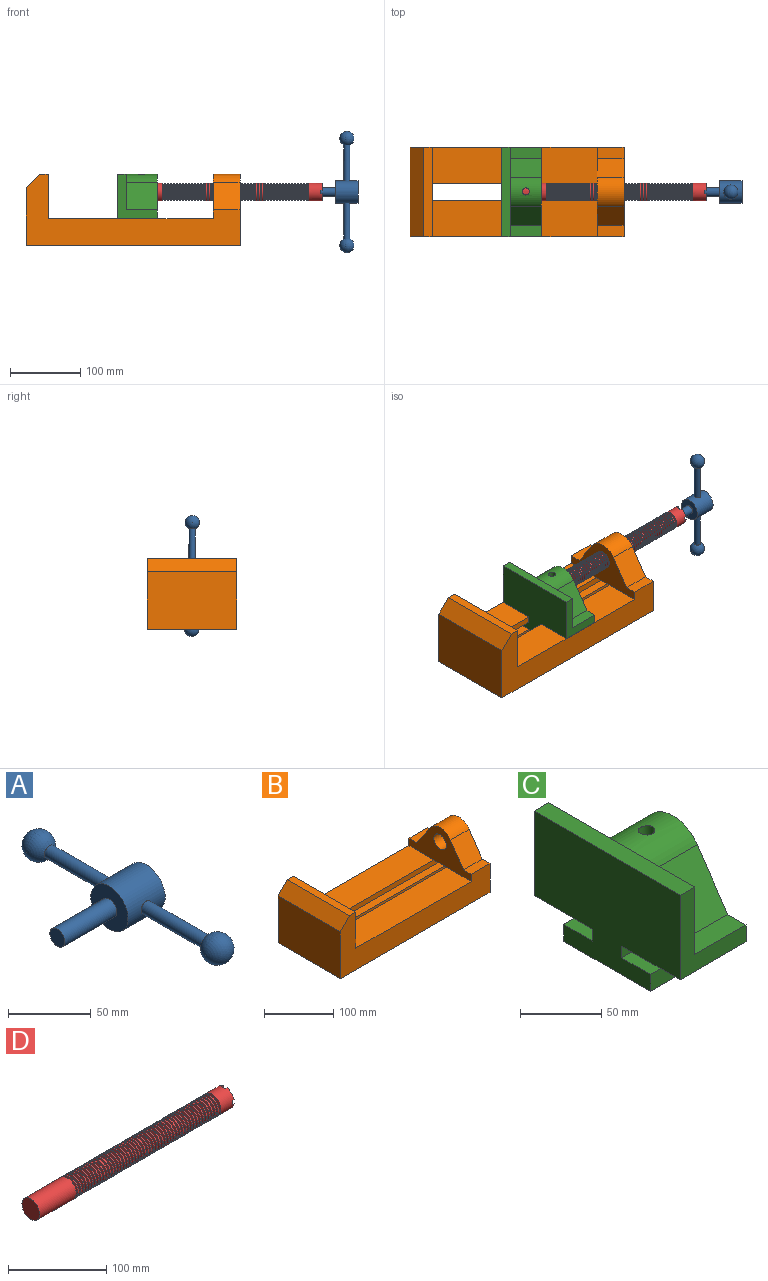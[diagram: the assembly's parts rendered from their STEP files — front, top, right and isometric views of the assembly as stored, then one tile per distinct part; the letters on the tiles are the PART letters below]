
ASSEMBLY  parts=4 mates=3
PART A: 13 faces, bbox 76.2x172.7x31.8 mm
  f0: cylinder r=4.45mm len=51.82mm, axis (0,1,0), area 1438.5mm2, adj f1,f8
  f1: cylinder r=15.88mm len=31.75mm, axis (-1,0,0), area 3041.6mm2, adj f0,f4,f5,f6
  f2: cylinder r=6.35mm len=44.45mm, axis (-1,0,0), area 1773.5mm2, adj f3,f5
  f3: plane 12.7x12.7mm, normal (-1,0,0), area 126.7mm2, adj f2
  f4: plane 31.75x31.75mm, normal (1,0,0), area 791.7mm2, adj f1
  f5: plane 31.75x31.75mm, normal (-1,0,0), area 665.1mm2, adj f1,f2
  f6: cylinder r=4.45mm len=51.82mm, axis (0,1,0), area 1438.5mm2, adj f1,f7
  f7: sphere r=10.16mm, area 1231.8mm2, adj f6
  f8: sphere r=10.16mm, area 1231.8mm2, adj f0
  f9: sphere r=4.45mm, area 124.1mm2, adj f10
  f10: plane 8.89x8.89mm, normal (0,-1,0), area 62.1mm2, adj f9
  f11: sphere r=4.45mm, area 124.1mm2, adj f12
  f12: plane 8.89x8.89mm, normal (0,1,0), area 62.1mm2, adj f11
PART B: 28 faces, bbox 304.8x127x101.6 mm
  f0: plane 234.95x50.8mm, normal (0,0,1), area 11935.5mm2, adj f5,f9,f16,f22
  f1: plane 234.95x50.8mm, normal (0,0,1), area 11935.5mm2, adj f5,f8,f16,f23
  f2: plane 127x82.55mm, normal (-1,0,0), area 10483.8mm2, adj f3,f7,f8,f9
  f3: plane 304.8x127mm, normal (0,0,-1), area 31774.1mm2, adj f2,f4,f5,f8,f9,f18,f27
  f4: plane 127x101.27mm, normal (1,0,0), area 7370.6mm2, adj f3,f8,f9,f10,f11,f12,f13,f14
  f5: plane 127x101.6mm, normal (1,0,0), area 9667.6mm2, adj f0,f1,f3,f6,f8,f9,f18,f19
  f6: plane 127x12.7mm, normal (0,0,1), area 1612.9mm2, adj f5,f7,f8,f9
  f7: plane 127x19.05mm, normal (-0.71,0,0.71), area 3421.5mm2, adj f2,f6,f8,f9
  f8: plane 304.8x101.6mm, normal (0,-1,0), area 13931.4mm2, adj f1,f2,f3,f4,f5,f6,f7,f14
  f9: plane 304.8x101.6mm, normal (0,1,0), area 13931.4mm2, adj f0,f2,f3,f4,f5,f6,f7,f10
  f10: plane 38.1x15.91mm, normal (0,0,1), area 606.2mm2, adj f4,f9,f11,f16
  f11: plane 39.29x38.1mm, normal (0,0.83,0.56), area 1807mm2, adj f4,f10,f12,f16
  f12: cylinder r=25.4mm len=42.08mm, axis (1,0,0), area 1889.1mm2, adj f4,f11,f13,f16
  f13: plane 39.31x38.1mm, normal (0,-0.83,0.56), area 1808.6mm2, adj f4,f12,f14,f16
  f14: plane 38.1x15.84mm, normal (0,0,1), area 603.5mm2, adj f4,f8,f13,f16
  f15: cylinder r=12.7mm len=38.1mm, axis (1,0,0), area 3040.2mm2, adj f4,f16
  f16: plane 127x63.17mm, normal (-1,0,0), area 4135mm2, adj f0,f1,f8,f9,f10,f11,f12,f13
  f17: plane 38.1x25.4mm, normal (0,0,-1), area 967.7mm2, adj f4,f16,f22,f23
  f18: plane 273.05x16.51mm, normal (0,-1,0), area 4508.1mm2, adj f3,f4,f5,f19
  f19: plane 273.05x25.02mm, normal (0,0,1), area 6830.5mm2, adj f4,f5,f18,f20
  f20: plane 273.05x12.7mm, normal (0,-1,0), area 3467.7mm2, adj f4,f5,f19,f21
  f21: plane 273.05x25.02mm, normal (0,0,-1), area 6830.5mm2, adj f4,f5,f20,f22
  f22: plane 273.05x8.89mm, normal (0,-1,0), area 2427.4mm2, adj f0,f4,f5,f17,f21
  f23: plane 273.05x8.89mm, normal (0,1,0), area 2427.4mm2, adj f1,f4,f5,f17,f24
  f24: plane 273.05x25.02mm, normal (0,0,-1), area 6830.5mm2, adj f4,f5,f23,f25
  f25: plane 273.05x12.7mm, normal (0,1,0), area 3467.7mm2, adj f4,f5,f24,f26
  f26: plane 273.05x25.02mm, normal (0,0,1), area 6830.5mm2, adj f4,f5,f25,f27
  f27: plane 273.05x16.51mm, normal (0,1,0), area 4508.1mm2, adj f3,f4,f5,f26
PART C: 23 faces, bbox 57.2x127x85.1 mm
  f0: plane 57.15x50.8mm, normal (0,0,-1), area 2903.2mm2, adj f3,f7,f8,f16
  f1: plane 44.45x15.91mm, normal (0,0,1), area 707.2mm2, adj f3,f5,f9,f11
  f2: plane 57.15x50.8mm, normal (0,0,-1), area 2903.2mm2, adj f3,f7,f9,f22
  f3: plane 127x84.76mm, normal (1,0,0), area 5318.8mm2, adj f0,f1,f2,f4,f8,f9,f10,f11
  f4: plane 44.45x15.84mm, normal (0,0,1), area 704mm2, adj f3,f5,f8,f10
  f5: plane 127x50.8mm, normal (1,0,0), area 3422.8mm2, adj f1,f4,f6,f8,f9,f10,f11,f13
  f6: plane 127x12.7mm, normal (0,0,1), area 1612.9mm2, adj f5,f7,f8,f9
  f7: plane 127x85.09mm, normal (-1,0,0), area 9248.3mm2, adj f0,f2,f6,f8,f9,f16,f17,f18
  f8: plane 63.5x57.15mm, normal (0,-1,0), area 1371mm2, adj f0,f3,f4,f5,f6,f7
  f9: plane 63.5x57.15mm, normal (0,1,0), area 1371mm2, adj f1,f2,f3,f5,f6,f7
  f10: plane 44.45x39.31mm, normal (0,-0.83,0.56), area 2110mm2, adj f3,f4,f5,f13
  f11: plane 44.45x39.29mm, normal (0,0.83,0.56), area 2108.2mm2, adj f1,f3,f5,f13
  f12: cylinder r=12.7mm len=44.45mm, axis (1,0,0), area 3463.8mm2, adj f3,f14,f15
  f13: cylinder r=25.4mm len=44.45mm, axis (1,0,0), area 2122.5mm2, adj f3,f5,f10,f11,f15
  f14: plane 25.4x25.4mm, normal (1,0,0), area 506.7mm2, adj f12
  f15: cylinder r=5.08mm len=13.76mm, axis (0,0,1), area 403.7mm2, adj f12,f13
  f16: plane 57.15x8.89mm, normal (0,-1,0), area 508.1mm2, adj f0,f3,f7,f17
  f17: plane 57.15x25.02mm, normal (0,0,1), area 1429.6mm2, adj f3,f7,f16,f18
  f18: plane 57.15x12.7mm, normal (0,-1,0), area 725.8mm2, adj f3,f7,f17,f19
  f19: plane 75.43x57.15mm, normal (0,0,-1), area 4310.9mm2, adj f3,f7,f18,f20
  f20: plane 57.15x12.7mm, normal (0,1,0), area 725.8mm2, adj f3,f7,f19,f21
  f21: plane 57.15x25.02mm, normal (0,0,1), area 1429.6mm2, adj f3,f7,f20,f22
  f22: plane 57.15x8.89mm, normal (0,1,0), area 508.1mm2, adj f2,f3,f7,f21
PART D: 220 faces, bbox 279.4x25.4x25.4 mm
  f0: cylinder r=12.7mm len=25.4mm, axis (-1,0,0), area 1468.2mm2, adj f1,f2,f3,f4,f7,f208,f209,f210
  f1: plane 9.9x9.9mm, normal (1,0,0), area 62.3mm2, adj f0,f5,f215,f217
  f2: plane 9.9x9.9mm, normal (1,0,0), area 62.3mm2, adj f0,f5,f209,f218
  f3: plane 9.9x9.9mm, normal (1,0,0), area 62.3mm2, adj f0,f5,f211,f214
  f4: plane 9.9x9.9mm, normal (1,0,0), area 62.3mm2, adj f0,f5,f208,f212
  f5: cylinder r=6.35mm len=25.4mm, axis (1,0,0), area 960.3mm2, adj f1,f2,f3,f4,f6,f208,f209,f210
  f6: plane 12.7x12.7mm, normal (1,0,0), area 126.7mm2, adj f5
  f7: cone r=12.7mm half-angle=76deg, axis (1,0,0), area 188mm2, adj f0,f9
  f8: cone r=12.7mm half-angle=76deg, axis (-1,0,0), area 188mm2, adj f9,f10
  f9: cylinder r=10.16mm len=20.32mm, axis (1,0,0), area 81.1mm2, adj f7,f8
  f10: cylinder r=12.7mm len=25.4mm, axis (-1,0,0), area 131.7mm2, adj f8,f11
  f11: cone r=12.7mm half-angle=76deg, axis (1,0,0), area 188mm2, adj f10,f13
  f12: cone r=12.7mm half-angle=76deg, axis (-1,0,0), area 188mm2, adj f13,f14
  f13: cylinder r=10.16mm len=20.32mm, axis (1,0,0), area 81.1mm2, adj f11,f12
  f14: cylinder r=12.7mm len=25.4mm, axis (-1,0,0), area 131.7mm2, adj f12,f15
  f15: cone r=12.7mm half-angle=76deg, axis (1,0,0), area 188mm2, adj f14,f17
  f16: cone r=12.7mm half-angle=76deg, axis (-1,0,0), area 188mm2, adj f17,f18
  f17: cylinder r=10.16mm len=20.32mm, axis (1,0,0), area 81.1mm2, adj f15,f16
  f18: cylinder r=12.7mm len=25.4mm, axis (-1,0,0), area 131.7mm2, adj f16,f19
  f19: cone r=12.7mm half-angle=76deg, axis (1,0,0), area 188mm2, adj f18,f21
  f20: cone r=12.7mm half-angle=76deg, axis (-1,0,0), area 188mm2, adj f21,f22
  f21: cylinder r=10.16mm len=20.32mm, axis (1,0,0), area 81.1mm2, adj f19,f20
  f22: cylinder r=12.7mm len=25.4mm, axis (-1,0,0), area 131.7mm2, adj f20,f23
  f23: cone r=12.7mm half-angle=76deg, axis (1,0,0), area 188mm2, adj f22,f25
  f24: cone r=12.7mm half-angle=76deg, axis (-1,0,0), area 188mm2, adj f25,f26
  f25: cylinder r=10.16mm len=20.32mm, axis (1,0,0), area 81.1mm2, adj f23,f24
  f26: cylinder r=12.7mm len=25.4mm, axis (-1,0,0), area 131.7mm2, adj f24,f27
  f27: cone r=12.7mm half-angle=76deg, axis (1,0,0), area 188mm2, adj f26,f29
  f28: cone r=12.7mm half-angle=76deg, axis (-1,0,0), area 188mm2, adj f29,f30
  f29: cylinder r=10.16mm len=20.32mm, axis (1,0,0), area 81.1mm2, adj f27,f28
  f30: cylinder r=12.7mm len=25.4mm, axis (-1,0,0), area 131.7mm2, adj f28,f31
  f31: cone r=12.7mm half-angle=76deg, axis (1,0,0), area 188mm2, adj f30,f33
  f32: cone r=12.7mm half-angle=76deg, axis (-1,0,0), area 188mm2, adj f33,f34
  f33: cylinder r=10.16mm len=20.32mm, axis (1,0,0), area 81.1mm2, adj f31,f32
  f34: cylinder r=12.7mm len=25.4mm, axis (-1,0,0), area 131.7mm2, adj f32,f35
  f35: cone r=12.7mm half-angle=76deg, axis (1,0,0), area 188mm2, adj f34,f37
  f36: cone r=12.7mm half-angle=76deg, axis (-1,0,0), area 188mm2, adj f37,f38
  f37: cylinder r=10.16mm len=20.32mm, axis (1,0,0), area 81.1mm2, adj f35,f36
  f38: cylinder r=12.7mm len=25.4mm, axis (-1,0,0), area 131.7mm2, adj f36,f39
  f39: cone r=12.7mm half-angle=76deg, axis (1,0,0), area 188mm2, adj f38,f41
  f40: cone r=12.7mm half-angle=76deg, axis (-1,0,0), area 188mm2, adj f41,f42
  f41: cylinder r=10.16mm len=20.32mm, axis (1,0,0), area 81.1mm2, adj f39,f40
  f42: cylinder r=12.7mm len=25.4mm, axis (-1,0,0), area 131.7mm2, adj f40,f43
  f43: cone r=12.7mm half-angle=76deg, axis (1,0,0), area 188mm2, adj f42,f45
  f44: cone r=12.7mm half-angle=76deg, axis (-1,0,0), area 188mm2, adj f45,f46
  f45: cylinder r=10.16mm len=20.32mm, axis (1,0,0), area 81.1mm2, adj f43,f44
  f46: cylinder r=12.7mm len=25.4mm, axis (-1,0,0), area 131.7mm2, adj f44,f47
  f47: cone r=12.7mm half-angle=76deg, axis (1,0,0), area 188mm2, adj f46,f49
  f48: cone r=12.7mm half-angle=76deg, axis (-1,0,0), area 188mm2, adj f49,f50
  f49: cylinder r=10.16mm len=20.32mm, axis (1,0,0), area 81.1mm2, adj f47,f48
  f50: cylinder r=12.7mm len=25.4mm, axis (-1,0,0), area 131.7mm2, adj f48,f51
  f51: cone r=12.7mm half-angle=76deg, axis (1,0,0), area 188mm2, adj f50,f53
  f52: cone r=12.7mm half-angle=76deg, axis (-1,0,0), area 188mm2, adj f53,f54
  f53: cylinder r=10.16mm len=20.32mm, axis (1,0,0), area 81.1mm2, adj f51,f52
  f54: cylinder r=12.7mm len=25.4mm, axis (-1,0,0), area 131.7mm2, adj f52,f55
  f55: cone r=12.7mm half-angle=76deg, axis (1,0,0), area 188mm2, adj f54,f57
  f56: cone r=12.7mm half-angle=76deg, axis (-1,0,0), area 188mm2, adj f57,f58
  f57: cylinder r=10.16mm len=20.32mm, axis (1,0,0), area 81.1mm2, adj f55,f56
  f58: cylinder r=12.7mm len=25.4mm, axis (-1,0,0), area 131.7mm2, adj f56,f59
  f59: cone r=12.7mm half-angle=76deg, axis (1,0,0), area 188mm2, adj f58,f61
  f60: cone r=12.7mm half-angle=76deg, axis (-1,0,0), area 188mm2, adj f61,f62
  f61: cylinder r=10.16mm len=20.32mm, axis (1,0,0), area 81.1mm2, adj f59,f60
  f62: cylinder r=12.7mm len=25.4mm, axis (-1,0,0), area 131.7mm2, adj f60,f63
  f63: cone r=12.7mm half-angle=76deg, axis (1,0,0), area 188mm2, adj f62,f65
  f64: cone r=12.7mm half-angle=76deg, axis (-1,0,0), area 188mm2, adj f65,f66
  f65: cylinder r=10.16mm len=20.32mm, axis (1,0,0), area 81.1mm2, adj f63,f64
  f66: cylinder r=12.7mm len=25.4mm, axis (-1,0,0), area 131.7mm2, adj f64,f67
  f67: cone r=12.7mm half-angle=76deg, axis (1,0,0), area 188mm2, adj f66,f69
  f68: cone r=12.7mm half-angle=76deg, axis (-1,0,0), area 188mm2, adj f69,f70
  f69: cylinder r=10.16mm len=20.32mm, axis (1,0,0), area 81.1mm2, adj f67,f68
  f70: cylinder r=12.7mm len=25.4mm, axis (-1,0,0), area 131.7mm2, adj f68,f71
  f71: cone r=12.7mm half-angle=76deg, axis (1,0,0), area 188mm2, adj f70,f73
  f72: cone r=12.7mm half-angle=76deg, axis (-1,0,0), area 188mm2, adj f73,f74
  f73: cylinder r=10.16mm len=20.32mm, axis (1,0,0), area 81.1mm2, adj f71,f72
  f74: cylinder r=12.7mm len=25.4mm, axis (-1,0,0), area 131.7mm2, adj f72,f75
  f75: cone r=12.7mm half-angle=76deg, axis (1,0,0), area 188mm2, adj f74,f77
  f76: cone r=12.7mm half-angle=76deg, axis (-1,0,0), area 188mm2, adj f77,f78
  f77: cylinder r=10.16mm len=20.32mm, axis (1,0,0), area 81.1mm2, adj f75,f76
  f78: cylinder r=12.7mm len=25.4mm, axis (-1,0,0), area 131.7mm2, adj f76,f79
  f79: cone r=12.7mm half-angle=76deg, axis (1,0,0), area 188mm2, adj f78,f81
  f80: cone r=12.7mm half-angle=76deg, axis (-1,0,0), area 188mm2, adj f81,f82
  f81: cylinder r=10.16mm len=20.32mm, axis (1,0,0), area 81.1mm2, adj f79,f80
  f82: cylinder r=12.7mm len=25.4mm, axis (-1,0,0), area 131.7mm2, adj f80,f83
  f83: cone r=12.7mm half-angle=76deg, axis (1,0,0), area 188mm2, adj f82,f85
  f84: cone r=12.7mm half-angle=76deg, axis (-1,0,0), area 188mm2, adj f85,f86
  f85: cylinder r=10.16mm len=20.32mm, axis (1,0,0), area 81.1mm2, adj f83,f84
  f86: cylinder r=12.7mm len=25.4mm, axis (-1,0,0), area 131.7mm2, adj f84,f87
  f87: cone r=12.7mm half-angle=76deg, axis (1,0,0), area 188mm2, adj f86,f89
  f88: cone r=12.7mm half-angle=76deg, axis (-1,0,0), area 188mm2, adj f89,f90
  f89: cylinder r=10.16mm len=20.32mm, axis (1,0,0), area 81.1mm2, adj f87,f88
  f90: cylinder r=12.7mm len=25.4mm, axis (-1,0,0), area 131.7mm2, adj f88,f91
  f91: cone r=12.7mm half-angle=76deg, axis (1,0,0), area 188mm2, adj f90,f93
  f92: cone r=12.7mm half-angle=76deg, axis (-1,0,0), area 188mm2, adj f93,f94
  f93: cylinder r=10.16mm len=20.32mm, axis (1,0,0), area 81.1mm2, adj f91,f92
  f94: cylinder r=12.7mm len=25.4mm, axis (-1,0,0), area 131.7mm2, adj f92,f95
  f95: cone r=12.7mm half-angle=76deg, axis (1,0,0), area 188mm2, adj f94,f97
  f96: cone r=12.7mm half-angle=76deg, axis (-1,0,0), area 188mm2, adj f97,f98
  f97: cylinder r=10.16mm len=20.32mm, axis (1,0,0), area 81.1mm2, adj f95,f96
  f98: cylinder r=12.7mm len=25.4mm, axis (-1,0,0), area 131.7mm2, adj f96,f99
  f99: cone r=12.7mm half-angle=76deg, axis (1,0,0), area 188mm2, adj f98,f101
  f100: cone r=12.7mm half-angle=76deg, axis (-1,0,0), area 188mm2, adj f101,f102
  f101: cylinder r=10.16mm len=20.32mm, axis (1,0,0), area 81.1mm2, adj f99,f100
  f102: cylinder r=12.7mm len=25.4mm, axis (-1,0,0), area 131.7mm2, adj f100,f103
  f103: cone r=12.7mm half-angle=76deg, axis (1,0,0), area 188mm2, adj f102,f105
  f104: cone r=12.7mm half-angle=76deg, axis (-1,0,0), area 188mm2, adj f105,f106
  f105: cylinder r=10.16mm len=20.32mm, axis (1,0,0), area 81.1mm2, adj f103,f104
  f106: cylinder r=12.7mm len=25.4mm, axis (-1,0,0), area 131.7mm2, adj f104,f107
  f107: cone r=12.7mm half-angle=76deg, axis (1,0,0), area 188mm2, adj f106,f109
  f108: cone r=12.7mm half-angle=76deg, axis (-1,0,0), area 188mm2, adj f109,f110
  f109: cylinder r=10.16mm len=20.32mm, axis (1,0,0), area 81.1mm2, adj f107,f108
  f110: cylinder r=12.7mm len=25.4mm, axis (-1,0,0), area 131.7mm2, adj f108,f111
  f111: cone r=12.7mm half-angle=76deg, axis (1,0,0), area 188mm2, adj f110,f113
  f112: cone r=12.7mm half-angle=76deg, axis (-1,0,0), area 188mm2, adj f113,f114
  f113: cylinder r=10.16mm len=20.32mm, axis (1,0,0), area 81.1mm2, adj f111,f112
  f114: cylinder r=12.7mm len=25.4mm, axis (-1,0,0), area 131.7mm2, adj f112,f115
  f115: cone r=12.7mm half-angle=76deg, axis (1,0,0), area 188mm2, adj f114,f117
  f116: cone r=12.7mm half-angle=76deg, axis (-1,0,0), area 188mm2, adj f117,f118
  f117: cylinder r=10.16mm len=20.32mm, axis (1,0,0), area 81.1mm2, adj f115,f116
  f118: cylinder r=12.7mm len=25.4mm, axis (-1,0,0), area 131.7mm2, adj f116,f119
  f119: cone r=12.7mm half-angle=76deg, axis (1,0,0), area 188mm2, adj f118,f121
  f120: cone r=12.7mm half-angle=76deg, axis (-1,0,0), area 188mm2, adj f121,f122
  f121: cylinder r=10.16mm len=20.32mm, axis (1,0,0), area 81.1mm2, adj f119,f120
  f122: cylinder r=12.7mm len=25.4mm, axis (-1,0,0), area 131.7mm2, adj f120,f123
  f123: cone r=12.7mm half-angle=76deg, axis (1,0,0), area 188mm2, adj f122,f125
  f124: cone r=12.7mm half-angle=76deg, axis (-1,0,0), area 188mm2, adj f125,f126
  f125: cylinder r=10.16mm len=20.32mm, axis (1,0,0), area 81.1mm2, adj f123,f124
  f126: cylinder r=12.7mm len=25.4mm, axis (-1,0,0), area 131.7mm2, adj f124,f127
  f127: cone r=12.7mm half-angle=76deg, axis (1,0,0), area 188mm2, adj f126,f129
  f128: cone r=12.7mm half-angle=76deg, axis (-1,0,0), area 188mm2, adj f129,f130
  f129: cylinder r=10.16mm len=20.32mm, axis (1,0,0), area 81.1mm2, adj f127,f128
  f130: cylinder r=12.7mm len=25.4mm, axis (-1,0,0), area 131.7mm2, adj f128,f131
  f131: cone r=12.7mm half-angle=76deg, axis (1,0,0), area 188mm2, adj f130,f133
  f132: cone r=12.7mm half-angle=76deg, axis (-1,0,0), area 188mm2, adj f133,f134
  f133: cylinder r=10.16mm len=20.32mm, axis (1,0,0), area 81.1mm2, adj f131,f132
  f134: cylinder r=12.7mm len=25.4mm, axis (-1,0,0), area 131.7mm2, adj f132,f135
  f135: cone r=12.7mm half-angle=76deg, axis (1,0,0), area 188mm2, adj f134,f137
  f136: cone r=12.7mm half-angle=76deg, axis (-1,0,0), area 188mm2, adj f137,f138
  f137: cylinder r=10.16mm len=20.32mm, axis (1,0,0), area 81.1mm2, adj f135,f136
  f138: cylinder r=12.7mm len=25.4mm, axis (-1,0,0), area 131.7mm2, adj f136,f139
  f139: cone r=12.7mm half-angle=76deg, axis (1,0,0), area 188mm2, adj f138,f141
  f140: cone r=12.7mm half-angle=76deg, axis (-1,0,0), area 188mm2, adj f141,f142
  f141: cylinder r=10.16mm len=20.32mm, axis (1,0,0), area 81.1mm2, adj f139,f140
  f142: cylinder r=12.7mm len=25.4mm, axis (-1,0,0), area 131.7mm2, adj f140,f143
  f143: cone r=12.7mm half-angle=76deg, axis (1,0,0), area 188mm2, adj f142,f145
  f144: cone r=12.7mm half-angle=76deg, axis (-1,0,0), area 188mm2, adj f145,f146
  f145: cylinder r=10.16mm len=20.32mm, axis (1,0,0), area 81.1mm2, adj f143,f144
  f146: cylinder r=12.7mm len=25.4mm, axis (-1,0,0), area 131.7mm2, adj f144,f147
  f147: cone r=12.7mm half-angle=76deg, axis (1,0,0), area 188mm2, adj f146,f149
  f148: cone r=12.7mm half-angle=76deg, axis (-1,0,0), area 188mm2, adj f149,f150
  f149: cylinder r=10.16mm len=20.32mm, axis (1,0,0), area 81.1mm2, adj f147,f148
  f150: cylinder r=12.7mm len=25.4mm, axis (-1,0,0), area 131.7mm2, adj f148,f151
  f151: cone r=12.7mm half-angle=76deg, axis (1,0,0), area 188mm2, adj f150,f153
  f152: cone r=12.7mm half-angle=76deg, axis (-1,0,0), area 188mm2, adj f153,f154
  f153: cylinder r=10.16mm len=20.32mm, axis (1,0,0), area 81.1mm2, adj f151,f152
  f154: cylinder r=12.7mm len=25.4mm, axis (-1,0,0), area 131.7mm2, adj f152,f155
  f155: cone r=12.7mm half-angle=76deg, axis (1,0,0), area 188mm2, adj f154,f157
  f156: cone r=12.7mm half-angle=76deg, axis (-1,0,0), area 188mm2, adj f157,f158
  f157: cylinder r=10.16mm len=20.32mm, axis (1,0,0), area 81.1mm2, adj f155,f156
  f158: cylinder r=12.7mm len=25.4mm, axis (-1,0,0), area 131.7mm2, adj f156,f159
  f159: cone r=12.7mm half-angle=76deg, axis (1,0,0), area 188mm2, adj f158,f161
  f160: cone r=12.7mm half-angle=76deg, axis (-1,0,0), area 188mm2, adj f161,f162
  f161: cylinder r=10.16mm len=20.32mm, axis (1,0,0), area 81.1mm2, adj f159,f160
  f162: cylinder r=12.7mm len=25.4mm, axis (-1,0,0), area 131.7mm2, adj f160,f163
  f163: cone r=12.7mm half-angle=76deg, axis (1,0,0), area 188mm2, adj f162,f165
  f164: cone r=12.7mm half-angle=76deg, axis (-1,0,0), area 188mm2, adj f165,f166
  f165: cylinder r=10.16mm len=20.32mm, axis (1,0,0), area 81.1mm2, adj f163,f164
  f166: cylinder r=12.7mm len=25.4mm, axis (-1,0,0), area 131.7mm2, adj f164,f167
  f167: cone r=12.7mm half-angle=76deg, axis (1,0,0), area 188mm2, adj f166,f169
  f168: cone r=12.7mm half-angle=76deg, axis (-1,0,0), area 188mm2, adj f169,f170
  f169: cylinder r=10.16mm len=20.32mm, axis (1,0,0), area 81.1mm2, adj f167,f168
  f170: cylinder r=12.7mm len=25.4mm, axis (-1,0,0), area 131.7mm2, adj f168,f171
  f171: cone r=12.7mm half-angle=76deg, axis (1,0,0), area 188mm2, adj f170,f173
  f172: cone r=12.7mm half-angle=76deg, axis (-1,0,0), area 188mm2, adj f173,f174
  f173: cylinder r=10.16mm len=20.32mm, axis (1,0,0), area 81.1mm2, adj f171,f172
  f174: cylinder r=12.7mm len=25.4mm, axis (-1,0,0), area 131.7mm2, adj f172,f175
  f175: cone r=12.7mm half-angle=76deg, axis (1,0,0), area 188mm2, adj f174,f177
  f176: cone r=12.7mm half-angle=76deg, axis (-1,0,0), area 188mm2, adj f177,f178
  f177: cylinder r=10.16mm len=20.32mm, axis (1,0,0), area 81.1mm2, adj f175,f176
  f178: cylinder r=12.7mm len=25.4mm, axis (-1,0,0), area 131.7mm2, adj f176,f179
  f179: cone r=12.7mm half-angle=76deg, axis (1,0,0), area 188mm2, adj f178,f181
  f180: cone r=12.7mm half-angle=76deg, axis (-1,0,0), area 188mm2, adj f181,f182
  f181: cylinder r=10.16mm len=20.32mm, axis (1,0,0), area 81.1mm2, adj f179,f180
  f182: cylinder r=12.7mm len=25.4mm, axis (-1,0,0), area 131.7mm2, adj f180,f183
  f183: cone r=12.7mm half-angle=76deg, axis (1,0,0), area 188mm2, adj f182,f185
  f184: cone r=12.7mm half-angle=76deg, axis (-1,0,0), area 188mm2, adj f185,f186
  f185: cylinder r=10.16mm len=20.32mm, axis (1,0,0), area 81.1mm2, adj f183,f184
  f186: cylinder r=12.7mm len=25.4mm, axis (-1,0,0), area 131.7mm2, adj f184,f187
  f187: cone r=12.7mm half-angle=76deg, axis (1,0,0), area 188mm2, adj f186,f189
  f188: cone r=12.7mm half-angle=76deg, axis (-1,0,0), area 188mm2, adj f189,f190
  f189: cylinder r=10.16mm len=20.32mm, axis (1,0,0), area 81.1mm2, adj f187,f188
  f190: cylinder r=12.7mm len=25.4mm, axis (-1,0,0), area 131.7mm2, adj f188,f191
  f191: cone r=12.7mm half-angle=76deg, axis (1,0,0), area 188mm2, adj f190,f193
  f192: cone r=12.7mm half-angle=76deg, axis (-1,0,0), area 188mm2, adj f193,f194
  f193: cylinder r=10.16mm len=20.32mm, axis (1,0,0), area 81.1mm2, adj f191,f192
  f194: cylinder r=12.7mm len=25.4mm, axis (-1,0,0), area 131.7mm2, adj f192,f195
  f195: cone r=12.7mm half-angle=76deg, axis (1,0,0), area 188mm2, adj f194,f197
  f196: cone r=12.7mm half-angle=76deg, axis (-1,0,0), area 188mm2, adj f197,f198
  f197: cylinder r=10.16mm len=20.32mm, axis (1,0,0), area 81.1mm2, adj f195,f196
  f198: cylinder r=12.7mm len=25.4mm, axis (-1,0,0), area 131.7mm2, adj f196,f199
  f199: cone r=12.7mm half-angle=76deg, axis (1,0,0), area 188mm2, adj f198,f201
  f200: cone r=12.7mm half-angle=76deg, axis (-1,0,0), area 188mm2, adj f201,f202
  f201: cylinder r=10.16mm len=20.32mm, axis (1,0,0), area 81.1mm2, adj f199,f200
  f202: cylinder r=12.7mm len=25.4mm, axis (-1,0,0), area 131.7mm2, adj f200,f203
  f203: cone r=12.7mm half-angle=76deg, axis (1,0,0), area 188mm2, adj f202,f205
  f204: cone r=12.7mm half-angle=76deg, axis (-1,0,0), area 188mm2, adj f205,f207
  f205: cylinder r=10.16mm len=20.32mm, axis (1,0,0), area 81.1mm2, adj f203,f204
  f206: plane 25.4x25.4mm, normal (-1,0,0), area 506.7mm2, adj f207
  f207: cylinder r=12.7mm len=52.45mm, axis (-1,0,0), area 4185.4mm2, adj f204,f206
  f208: plane 6.62x2.54mm, normal (0,0,1), area 16.8mm2, adj f0,f4,f5,f210
  f209: plane 6.62x2.54mm, normal (0,0,-1), area 16.8mm2, adj f0,f2,f5,f210
  f210: plane 6.88x5.08mm, normal (1,0,0), area 32.7mm2, adj f0,f5,f208,f209
  f211: plane 6.62x2.54mm, normal (0,-1,0), area 16.8mm2, adj f0,f3,f5,f213
  f212: plane 6.62x2.54mm, normal (0,1,0), area 16.8mm2, adj f0,f4,f5,f213
  f213: plane 6.88x5.08mm, normal (1,0,0), area 32.7mm2, adj f0,f5,f211,f212
  f214: plane 6.62x2.54mm, normal (0,0,1), area 16.8mm2, adj f0,f3,f5,f216
  f215: plane 6.62x2.54mm, normal (0,0,-1), area 16.8mm2, adj f0,f1,f5,f216
  f216: plane 6.88x5.08mm, normal (1,0,0), area 32.7mm2, adj f0,f5,f214,f215
  f217: plane 6.62x2.54mm, normal (0,-1,0), area 16.8mm2, adj f0,f1,f5,f219
  f218: plane 6.62x2.54mm, normal (0,1,0), area 16.8mm2, adj f0,f2,f5,f219
  f219: plane 6.88x5.08mm, normal (1,0,0), area 32.7mm2, adj f0,f5,f217,f218
PLACE A rot(axis=(1,0,0),90.2deg) t=(61.33,33.13,90.56)mm
PLACE B t=(-33.63,-43.07,14.08)mm fixed
PLACE C t=(64.5,-43.07,14.08)mm
PLACE D t=(64.5,-43.07,14.08)mm
MATE slider B.f5 <-> C.f7  axis (-1,0,0) through (-306.68,-106.57,52.18)mm
MATE fastened C.f12 <-> D.f5  axis (1,0,0) through (-195.85,-43.07,90.28)mm
MATE revolute D.f5 <-> A.f2  axis (1,0,0) through (58.15,-43.07,90.28)mm
